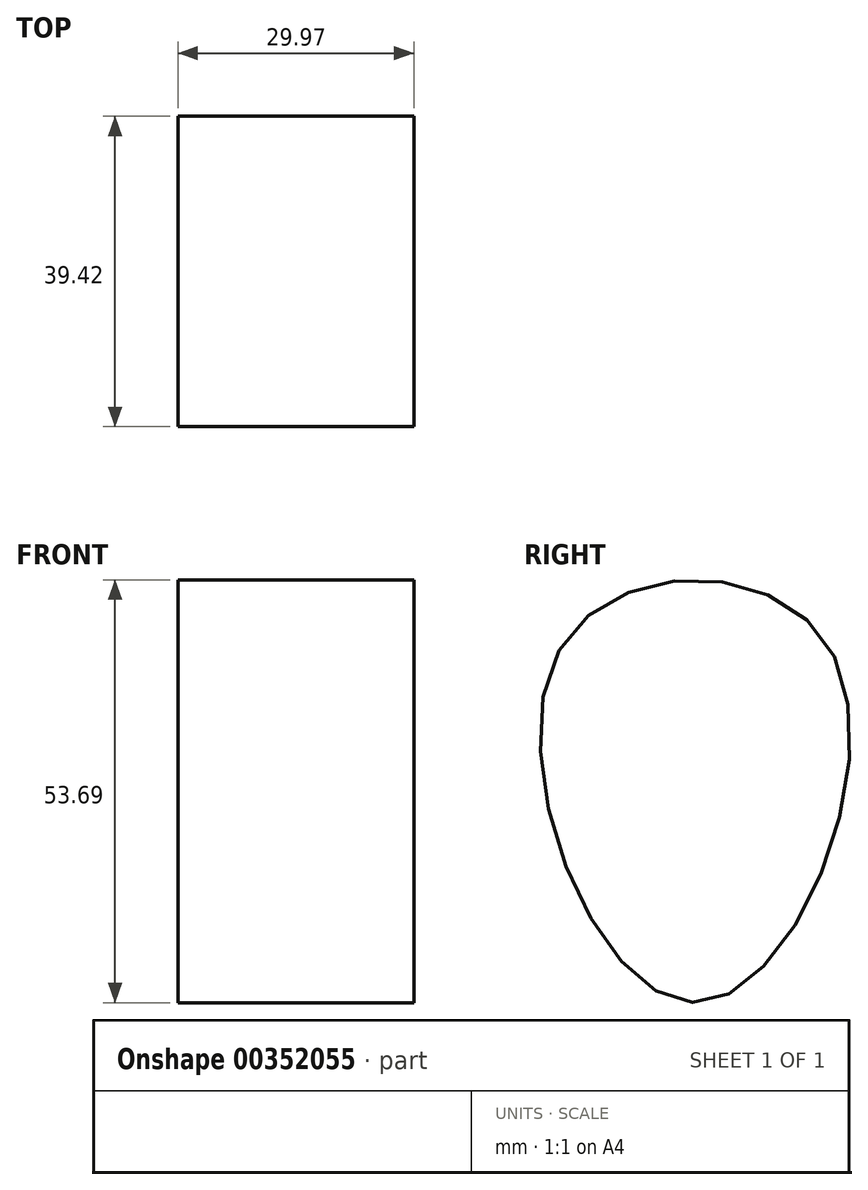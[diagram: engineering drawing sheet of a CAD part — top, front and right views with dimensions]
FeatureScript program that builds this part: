
annotation { "Feature Type Name" : "Feature", "Feature Type Description" : "" }
export const myFeature = defineFeature(function(context is Context, id is Id, definition is map)
    precondition{}
    {
        {
            var Q0;
            Q0=qCreatedBy(makeId("Right.planeOp"),FACE);
            var sketch = newSketch(context, id + "F0", { "sketchPlane" : qUnion([Q0])});
            skFitSpline(sketch, "E0", {"points": [v(-17.3, 44.72) * mm, v(17.3, 44.72) * mm, v(0, 0) * mm, v(-17.3, 44.72) * mm]});
            skSolve(sketch);
        }
        {
            var Q0;
            Q0=makeQuery(id+"F0.imprint","IMPRINT",FACE,{"disambiguationData":[TD([[makeQuery(id+"F0.imprint","IMPRINT",EDGE,{"derivedFrom":sQuery(id+"F0.wireOp",EDGE,"E0")}),-1.0]])]});
            extrude(context, id + "F1", {"entities" : qUnion([Q0]), "depth" : 29.97 * mm});
        }
    });
